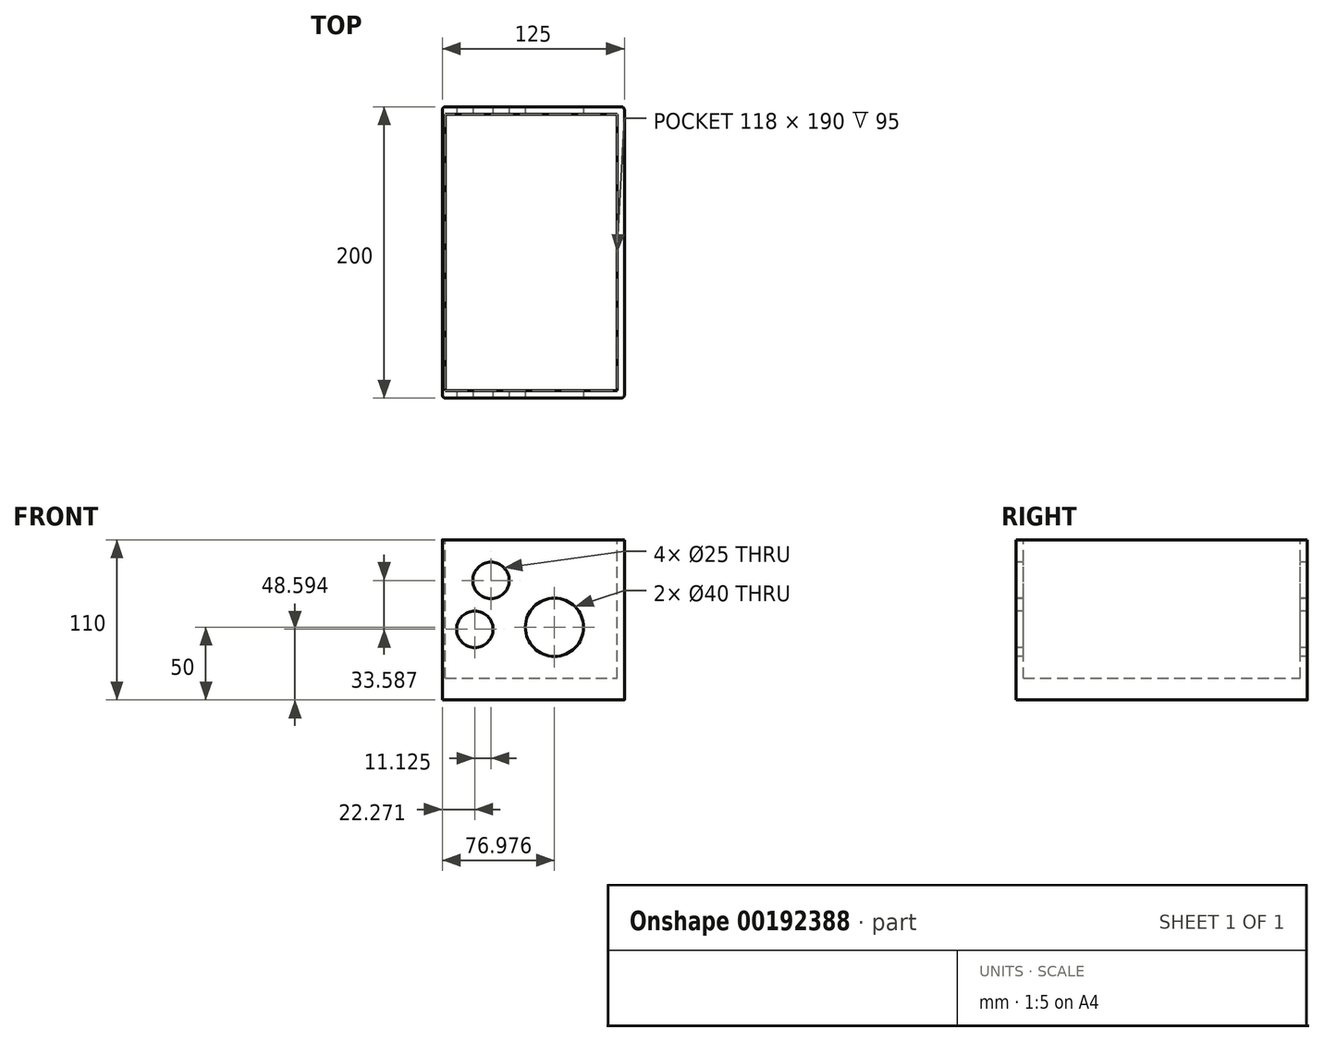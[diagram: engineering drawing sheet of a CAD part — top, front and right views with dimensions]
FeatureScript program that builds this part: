
annotation { "Feature Type Name" : "Feature", "Feature Type Description" : "" }
export const myFeature = defineFeature(function(context is Context, id is Id, definition is map)
    precondition{}
    {
        {
            var Q0;
            Q0=qCreatedBy(makeId("Front.planeOp"),FACE);
            var sketch = newSketch(context, id + "F0", { "sketchPlane" : qUnion([Q0])});
            skLineSegment(sketch, "E0", {"start": v(0, 0) * mm, "end": v(125, 0) * mm});
            skLineSegment(sketch, "E1", {"start": v(125, 0) * mm, "end": v(125, 110) * mm});
            skLineSegment(sketch, "E2", {"start": v(0, 110) * mm, "end": v(0, 0) * mm});
            skPoint(sketch, "E3.visualSharp", {"position": v(0, 120) * mm});
            skPoint(sketch, "E4.visualSharp", {"position": v(125, 120) * mm});
            skLineSegment(sketch, "E5", {"start": v(0, 110) * mm, "end": v(125, 110) * mm});
            skSolve(sketch);
        }
        {
            var Q0;
            Q0 = qSketchRegion(id + "F0", true);
            extrude(context, id + "F1", {"entities" : qUnion([Q0]), "depth" : 200 * mm});
        }
        {
            var Q0;
            Q0=makeQuery(id+"F1.opExtrude","SWEPT_FACE",FACE,{"disambiguationData":[OSD([sQuery(id+"F0.wireOp",EDGE,"E5")])]});
            var sketch = newSketch(context, id + "F2", { "sketchPlane" : qUnion([Q0])});
            skLineSegment(sketch, "E6.0", {"start": v(5, -195) * mm, "end": v(5, -5) * mm});
            skLineSegment(sketch, "E7.0", {"start": v(5, -5) * mm, "end": v(120, -5) * mm});
            skLineSegment(sketch, "E8.0", {"start": v(120, -195) * mm, "end": v(120, -5) * mm});
            skLineSegment(sketch, "E8.1", {"start": v(5, -195) * mm, "end": v(120, -195) * mm});
            skSolve(sketch);
        }
        {
            var Q0;
            Q0=makeQuery(id+"F2.imprint","IMPRINT",FACE,{"disambiguationData":[TD([[makeQuery(id+"F2.imprint","IMPRINT",EDGE,{"derivedFrom":sQuery(id+"F2.wireOp",EDGE,"E6.0")}),-1.0]])]});
            extrude(context, id + "F3", {"entities" : qUnion([Q0]), "operationType" : NewBodyOperationType.REMOVE, "oppositeDirection" : true, "depth" : 95 * mm});
        }
        {
            var Q0;
            Q0=makeQuery(id+"F1.opExtrude","CAP_EDGE",EDGE,{"disambiguationData":[OSD([sQuery(id+"F0.wireOp",EDGE,"E1")])],"isStart":true});
            var Q1;
            Q1=makeQuery(id+"F1.opExtrude","CAP_EDGE",EDGE,{"disambiguationData":[OSD([sQuery(id+"F0.wireOp",EDGE,"E2")])],"isStart":true});
            var Q2;
            Q2=makeQuery(id+"F1.opExtrude","CAP_EDGE",EDGE,{"disambiguationData":[OSD([sQuery(id+"F0.wireOp",EDGE,"E1")])],"isStart":false});
            var Q3;
            Q3=makeQuery(id+"F1.opExtrude","CAP_EDGE",EDGE,{"disambiguationData":[OSD([sQuery(id+"F0.wireOp",EDGE,"E2")])],"isStart":false});
            fillet(context, id + "F4", {"entities" : qUnion([Q0, Q1, Q2, Q3]), "radius" : 2 * mm, "tangentPropagation" : true, "allowEdgeOverflow" : false});
        }
        {
            var Q0;
            Q0=makeQuery(id+"F1.opExtrude","CAP_FACE",FACE,{"disambiguationData":[OSD([sQuery(id+"F0.wireOp",EDGE,"E0"),sQuery(id+"F0.wireOp",EDGE,"E1"),sQuery(id+"F0.wireOp",EDGE,"E2"),sQuery(id+"F0.wireOp",EDGE,"E5")])],"isStart":false});
            var sketch = newSketch(context, id + "F5", { "sketchPlane" : qUnion([Q0])});
            skPoint(sketch, "E9.endSnap0", {"position": v(62.5, 110) * mm});
            skCircle(sketch, "E10", {"center": v(76.98, 50) * mm, "radius": 20 * mm});
            skSolve(sketch);
        }
        {
            var Q0;
            Q0=makeQuery(id+"F1.opExtrude","CAP_FACE",FACE,{"disambiguationData":[OSD([sQuery(id+"F0.wireOp",EDGE,"E0"),sQuery(id+"F0.wireOp",EDGE,"E1"),sQuery(id+"F0.wireOp",EDGE,"E2"),sQuery(id+"F0.wireOp",EDGE,"E5")])],"isStart":false});
            var sketch = newSketch(context, id + "F6", { "sketchPlane" : qUnion([Q0])});
            skCircle(sketch, "E11", {"center": v(22.27, 48.6) * mm, "radius": 12.5 * mm});
            skCircle(sketch, "E12", {"center": v(33.4, 82.18) * mm, "radius": 12.5 * mm});
            skSolve(sketch);
        }
        {
            var Q0;
            Q0 = qSketchRegion(id + "F5", true);
            extrude(context, id + "F7", {"entities" : qUnion([Q0]), "operationType" : NewBodyOperationType.REMOVE, "endBound" : BoundingType.THROUGH_ALL, "oppositeDirection" : true, "depth" : 25 * mm});
        }
        {
            var Q0;
            Q0 = qSketchRegion(id + "F6", true);
            extrude(context, id + "F8", {"entities" : qUnion([Q0]), "operationType" : NewBodyOperationType.REMOVE, "endBound" : BoundingType.THROUGH_ALL, "oppositeDirection" : true, "depth" : 25 * mm});
        }
        {
            var Q0;
            Q0=makeQuery(id+"F1.opExtrude","SWEPT_FACE",FACE,{"disambiguationData":[OSD([sQuery(id+"F0.wireOp",EDGE,"E5")])]});
            var sketch = newSketch(context, id + "F9", { "sketchPlane" : qUnion([Q0])});
            skLineSegment(sketch, "E13", {"start": v(5, -5) * mm, "end": v(2, -5) * mm});
            skLineSegment(sketch, "E14", {"start": v(2, -5) * mm, "end": v(2, -195) * mm});
            skLineSegment(sketch, "E15", {"start": v(2, -195) * mm, "end": v(5, -195) * mm});
            skLineSegment(sketch, "E16", {"start": v(5, -195) * mm, "end": v(5, -5) * mm});
            skSolve(sketch);
        }
        {
            var Q0;
            Q0 = qSketchRegion(id + "F9", true);
            var Q1;
            Q1=makeQuery(id+"F3.boolean.opBoolean","COPY",FACE,{"derivedFrom":makeQuery(id+"F3.opExtrude","CAP_FACE",FACE,{"disambiguationData":[OSD([sQuery(id+"F2.wireOp",EDGE,"E6.0"),sQuery(id+"F2.wireOp",EDGE,"E7.0"),sQuery(id+"F2.wireOp",EDGE,"E8.0"),sQuery(id+"F2.wireOp",EDGE,"E8.1")])],"isStart":false})});
            extrude(context, id + "F10", {"entities" : qUnion([Q0]), "operationType" : NewBodyOperationType.REMOVE, "endBound" : BoundingType.UP_TO_SURFACE, "oppositeDirection" : true, "endBoundEntityFace" : qUnion([Q1]), "depth" : 25 * mm});
        }
    });
